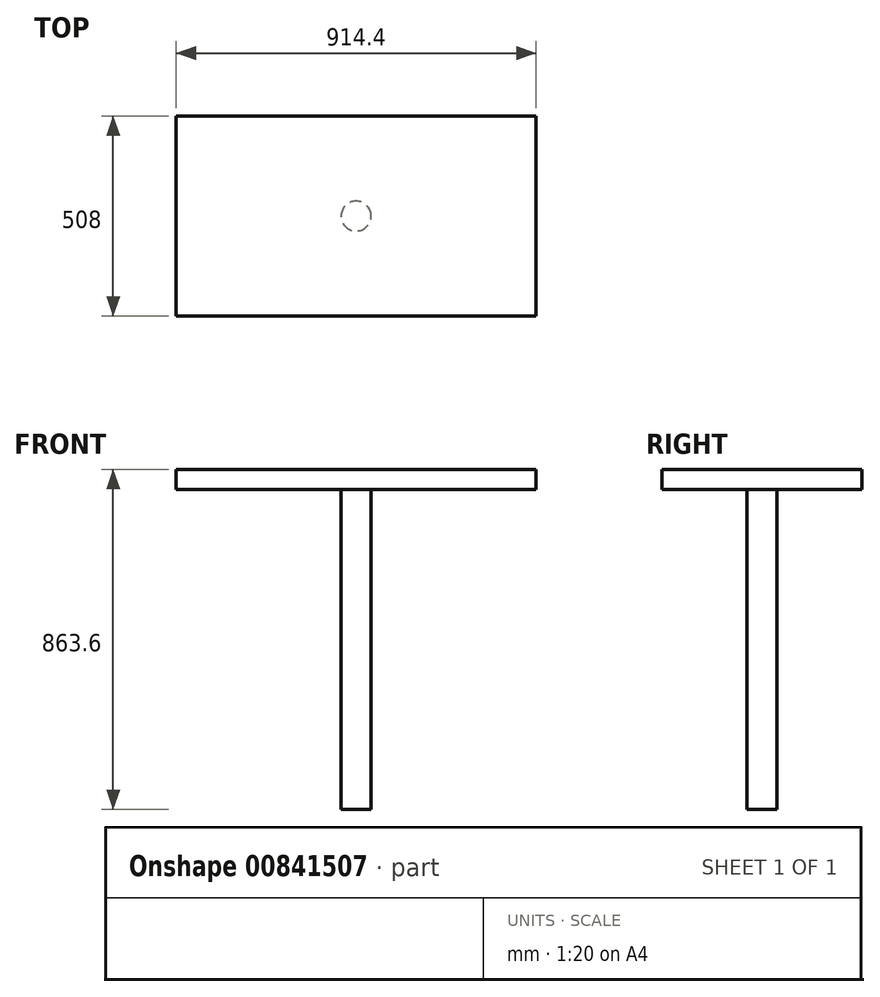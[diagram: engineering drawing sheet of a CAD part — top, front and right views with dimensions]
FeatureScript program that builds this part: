
annotation { "Feature Type Name" : "Feature", "Feature Type Description" : "" }
export const myFeature = defineFeature(function(context is Context, id is Id, definition is map)
    precondition{}
    {
        {
            var Q0;
            Q0=qCreatedBy(makeId("Top.planeOp"),FACE);
            var sketch = newSketch(context, id + "F0", { "sketchPlane" : qUnion([Q0])});
            skLineSegment(sketch, "E0.bottom", {"start": v(0, 0) * mm, "end": v(914.4, 0) * mm});
            skLineSegment(sketch, "E0.top", {"start": v(0, 508) * mm, "end": v(914.4, 508) * mm});
            skLineSegment(sketch, "E0.left", {"start": v(0, 0) * mm, "end": v(0, 508) * mm});
            skLineSegment(sketch, "E0.right", {"start": v(914.4, 0) * mm, "end": v(914.4, 508) * mm});
            skSolve(sketch);
        }
        {
            var Q0;
            Q0=qSketchRegion(id+"F0",true);
            extrude(context, id + "F1", {"entities" : qUnion([Q0]), "depth" : 50.8 * mm, "offsetDistance" : 25.4 * mm});
        }
        {
            var Q0;
            Q0=makeQuery(id+"F1.opExtrude","CAP_FACE",FACE,{"disambiguationData":[OSD([sQuery(id+"F0.wireOp",EDGE,"E0.bottom"),sQuery(id+"F0.wireOp",EDGE,"E0.top"),sQuery(id+"F0.wireOp",EDGE,"E0.left"),sQuery(id+"F0.wireOp",EDGE,"E0.right")])],"isStart":true});
            var sketch = newSketch(context, id + "F2", { "sketchPlane" : qUnion([Q0])});
            skLineSegment(sketch, "E1", {"start": v(457.2, -508) * mm, "end": v(457.2, 0) * mm, "construction": true});
            skLineSegment(sketch, "E2", {"start": v(914.4, -254) * mm, "end": v(0, -254) * mm, "construction": true});
            skPoint(sketch, "E3", {"position": v(457.2, -254) * mm});
            skCircle(sketch, "E4", {"center": v(457.2, -254) * mm, "radius": 38.1 * mm});
            skSolve(sketch);
        }
        {
            var Q0;
            Q0=qSketchRegion(id+"F2",true);
            extrude(context, id + "F3", {"entities" : qUnion([Q0]), "operationType" : NewBodyOperationType.ADD, "depth" : 812.8 * mm, "offsetDistance" : 25.4 * mm});
        }
    });
